# Revit family: 45
name_source: partatom
category: Pipe Accessories
revit_build: Autodesk Revit 2018 (Build: 20170223_1515(x64)
units: mm (PartAtom-declared; Revit-internal decimal feet)

## family parameters
Always vertical = Yes
Cut with Voids When Loaded = No
OmniClass Number = 23.27.43.00
OmniClass Title = Pipe Fittings
Part Type = Valve - Breaks Into
Round Connector Dimension = Use Diameter
Shared = No
Work Plane-Based = No

## types (2) — shared parameters
Assembly Code = D2040100
BIMobject category = Joints
Description = 2 Ways Inclined Manifold Valve-Female - 90664
Design country = Italy
Edition number = 1
IFC Classification = Pipe Fitting
Keynote = 15410
Manufacturer = Aignep Spa
Manufacturer country = Italy
Manufacturer name = Aignep Spa
Material main = Brass
Model = 90664
OmniClass Code = 23-27 43 00
OmniClass Description = Pipe Fittings
Product Guid = 4f65e8df-a141-4147-bf88-ad2dd1b95941
Product Material = AIGNEP - Brass - Yellow
Product SKU = 2-Ways-Inclined-Manifold-Valve-Female-90664
Product certification = https://www.aignep.com
Product data url = https://www.bimobject.com
Product family = INFINITY
Product group = Valves
Product name = 2 Ways Inclined Manifold Valve-Female - 90664
Product url = https://www.aignep.com
QR code = https://www.bimobject.com
URL = https://www.aignep.com

## type names (no varying parameters)
- D 20
- D 25

## geometry (parser evidence)
native form markers: Sweep x11
no freeform markers — native parametric forms only
